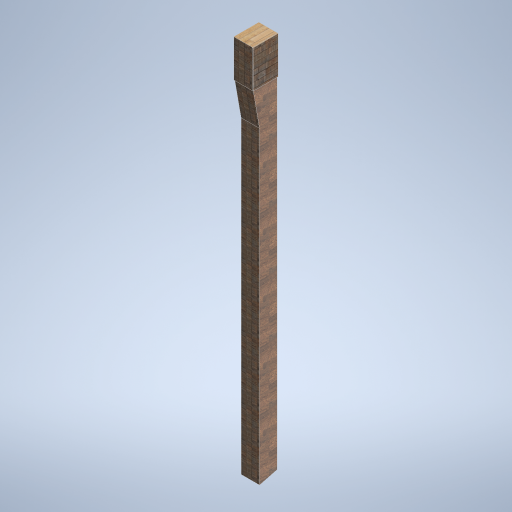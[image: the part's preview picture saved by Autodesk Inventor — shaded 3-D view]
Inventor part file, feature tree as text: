
AUTODESK INVENTOR PART (.ipt)
format: ipt  version: 2024.2 (Build 282272000, 272)  size: 321,024 bytes
history: native  units: in
note: dims shown in document units (in); Inventor stores cm internally (conversion verified against a paired STEP export)
features: other x3, sketch x1
ambient origin geometry x8: Origin, YZ Plane, XZ Plane, XY Plane, X Axis, Y Axis, Z Axis, Center Point
bodies: Solid1 (feature_tree)
feature tree (4):
  other  "side_pillar_02.ipt"
  other  "Solid1::side_pillar_02.ipt"
  other  "TaggingFeature1"
  sketch  "Sketch3"  dims[d0=0.3937in]
